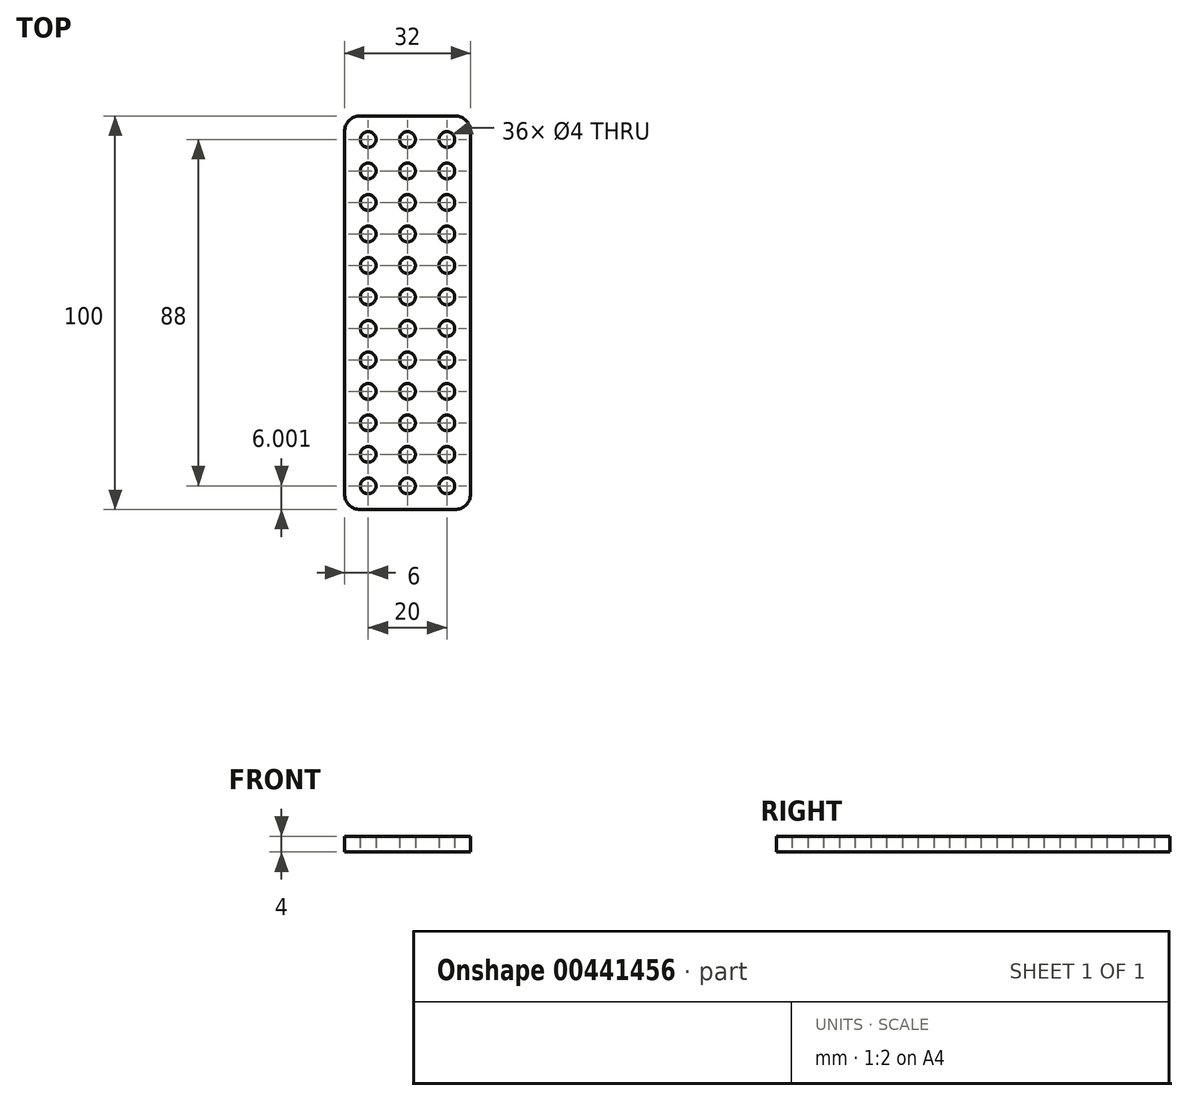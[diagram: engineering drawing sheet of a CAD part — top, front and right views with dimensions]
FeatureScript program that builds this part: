
annotation { "Feature Type Name" : "Feature", "Feature Type Description" : "" }
export const myFeature = defineFeature(function(context is Context, id is Id, definition is map)
    precondition{}
    {
        {
            var Q0;
            Q0=qCreatedBy(makeId("Top.planeOp"),FACE);
            var sketch = newSketch(context, id + "F0", { "sketchPlane" : qUnion([Q0])});
            skCircle(sketch, "E0", {"center": v(-26, 20.96) * mm, "radius": 2 * mm});
            skCircle(sketch, "E1.1.0.0", {"center": v(-16, 20.96) * mm, "radius": 2 * mm});
            skCircle(sketch, "E1.2.0.0", {"center": v(-6, 20.96) * mm, "radius": 2 * mm});
            skLineSegment(sketch, "E1.direction1", {"start": v(-26, 20.96) * mm, "end": v(-16, 20.96) * mm, "construction": true});
            skLineSegment(sketch, "E2.direction1", {"start": v(-26, 20.96) * mm, "end": v(-16.13, 20.96) * mm, "construction": true});
            skLineSegment(sketch, "E2.direction2", {"start": v(-26, 20.96) * mm, "end": v(-26, 28.96) * mm, "construction": true});
            skLineSegment(sketch, "E3.bottom", {"start": v(0, 114.96) * mm, "end": v(-32, 114.96) * mm});
            skLineSegment(sketch, "E3.top", {"start": v(0, 14.96) * mm, "end": v(-32, 14.96) * mm});
            skLineSegment(sketch, "E3.left", {"start": v(0, 114.96) * mm, "end": v(0, 14.96) * mm});
            skLineSegment(sketch, "E3.right", {"start": v(-32, 114.96) * mm, "end": v(-32, 14.96) * mm});
            skCircle(sketch, "E4.0.0.1", {"center": v(-26, 28.96) * mm, "radius": 2 * mm});
            skCircle(sketch, "E4.2.0.1", {"center": v(-16, 28.96) * mm, "radius": 2 * mm});
            skCircle(sketch, "E4.4.0.1", {"center": v(-6, 28.96) * mm, "radius": 2 * mm});
            skCircle(sketch, "E4.0.0.2", {"center": v(-26, 36.96) * mm, "radius": 2 * mm});
            skCircle(sketch, "E4.2.0.2", {"center": v(-16, 36.96) * mm, "radius": 2 * mm});
            skCircle(sketch, "E4.4.0.2", {"center": v(-6, 36.96) * mm, "radius": 2 * mm});
            skCircle(sketch, "E4.0.0.3", {"center": v(-26, 44.96) * mm, "radius": 2 * mm});
            skCircle(sketch, "E4.2.0.3", {"center": v(-16, 44.96) * mm, "radius": 2 * mm});
            skCircle(sketch, "E4.4.0.3", {"center": v(-6, 44.96) * mm, "radius": 2 * mm});
            skCircle(sketch, "E4.0.0.4", {"center": v(-26, 52.96) * mm, "radius": 2 * mm});
            skCircle(sketch, "E4.2.0.4", {"center": v(-16, 52.96) * mm, "radius": 2 * mm});
            skCircle(sketch, "E4.4.0.4", {"center": v(-6, 52.96) * mm, "radius": 2 * mm});
            skCircle(sketch, "E4.0.0.5", {"center": v(-26, 60.96) * mm, "radius": 2 * mm});
            skCircle(sketch, "E4.2.0.5", {"center": v(-16, 60.96) * mm, "radius": 2 * mm});
            skCircle(sketch, "E4.4.0.5", {"center": v(-6, 60.96) * mm, "radius": 2 * mm});
            skCircle(sketch, "E4.0.0.6", {"center": v(-26, 68.96) * mm, "radius": 2 * mm});
            skCircle(sketch, "E4.2.0.6", {"center": v(-16, 68.96) * mm, "radius": 2 * mm});
            skCircle(sketch, "E4.4.0.6", {"center": v(-6, 68.96) * mm, "radius": 2 * mm});
            skCircle(sketch, "E4.0.0.7", {"center": v(-26, 76.96) * mm, "radius": 2 * mm});
            skCircle(sketch, "E4.2.0.7", {"center": v(-16, 76.96) * mm, "radius": 2 * mm});
            skCircle(sketch, "E4.4.0.7", {"center": v(-6, 76.96) * mm, "radius": 2 * mm});
            skCircle(sketch, "E4.0.0.8", {"center": v(-26, 84.96) * mm, "radius": 2 * mm});
            skCircle(sketch, "E4.2.0.8", {"center": v(-16, 84.96) * mm, "radius": 2 * mm});
            skCircle(sketch, "E4.4.0.8", {"center": v(-6, 84.96) * mm, "radius": 2 * mm});
            skCircle(sketch, "E4.0.0.9", {"center": v(-26, 92.96) * mm, "radius": 2 * mm});
            skCircle(sketch, "E4.2.0.9", {"center": v(-16, 92.96) * mm, "radius": 2 * mm});
            skCircle(sketch, "E4.4.0.9", {"center": v(-6, 92.96) * mm, "radius": 2 * mm});
            skCircle(sketch, "E5.0.0.10", {"center": v(-26, 100.96) * mm, "radius": 2 * mm});
            skCircle(sketch, "E5.2.0.10", {"center": v(-16, 100.96) * mm, "radius": 2 * mm});
            skCircle(sketch, "E5.4.0.10", {"center": v(-6, 100.96) * mm, "radius": 2 * mm});
            skCircle(sketch, "E5.0.0.11", {"center": v(-26, 108.96) * mm, "radius": 2 * mm});
            skCircle(sketch, "E5.2.0.11", {"center": v(-16, 108.96) * mm, "radius": 2 * mm});
            skCircle(sketch, "E5.4.0.11", {"center": v(-6, 108.96) * mm, "radius": 2 * mm});
            skSolve(sketch);
        }
        {
            var Q0;
            Q0=makeQuery(id+"F0.imprint","IMPRINT",FACE,{"disambiguationData":[TD([[makeQuery(id+"F0.imprint","IMPRINT",EDGE,{"derivedFrom":sQuery(id+"F0.wireOp",EDGE,"E0")}),-1.0]])]});
            extrude(context, id + "F1", {"entities" : qUnion([Q0]), "depth" : 4 * mm, "offsetDistance" : 25 * mm});
        }
        {
            var Q0;
            Q0=makeQuery(id+"F1.opExtrude","SWEPT_EDGE",EDGE,{"disambiguationData":[OSD([sQuery(id+"F0.wireOp",EDGE,"E3.top"),sQuery(id+"F0.wireOp",EDGE,"E3.right")])]});
            var Q1;
            Q1=makeQuery(id+"F1.opExtrude","SWEPT_EDGE",EDGE,{"disambiguationData":[OSD([sQuery(id+"F0.wireOp",EDGE,"E3.top"),sQuery(id+"F0.wireOp",EDGE,"E3.left")])]});
            var Q2;
            Q2=makeQuery(id+"F1.opExtrude","SWEPT_EDGE",EDGE,{"disambiguationData":[OSD([sQuery(id+"F0.wireOp",EDGE,"E3.bottom"),sQuery(id+"F0.wireOp",EDGE,"E3.left")])]});
            var Q3;
            Q3=makeQuery(id+"F1.opExtrude","SWEPT_EDGE",EDGE,{"disambiguationData":[OSD([sQuery(id+"F0.wireOp",EDGE,"E3.bottom"),sQuery(id+"F0.wireOp",EDGE,"E3.right")])]});
            fillet(context, id + "F2", {"entities" : qUnion([Q0, Q1, Q2, Q3]), "radius" : 4 * mm, "tangentPropagation" : true, "allowEdgeOverflow" : false});
        }
    });
